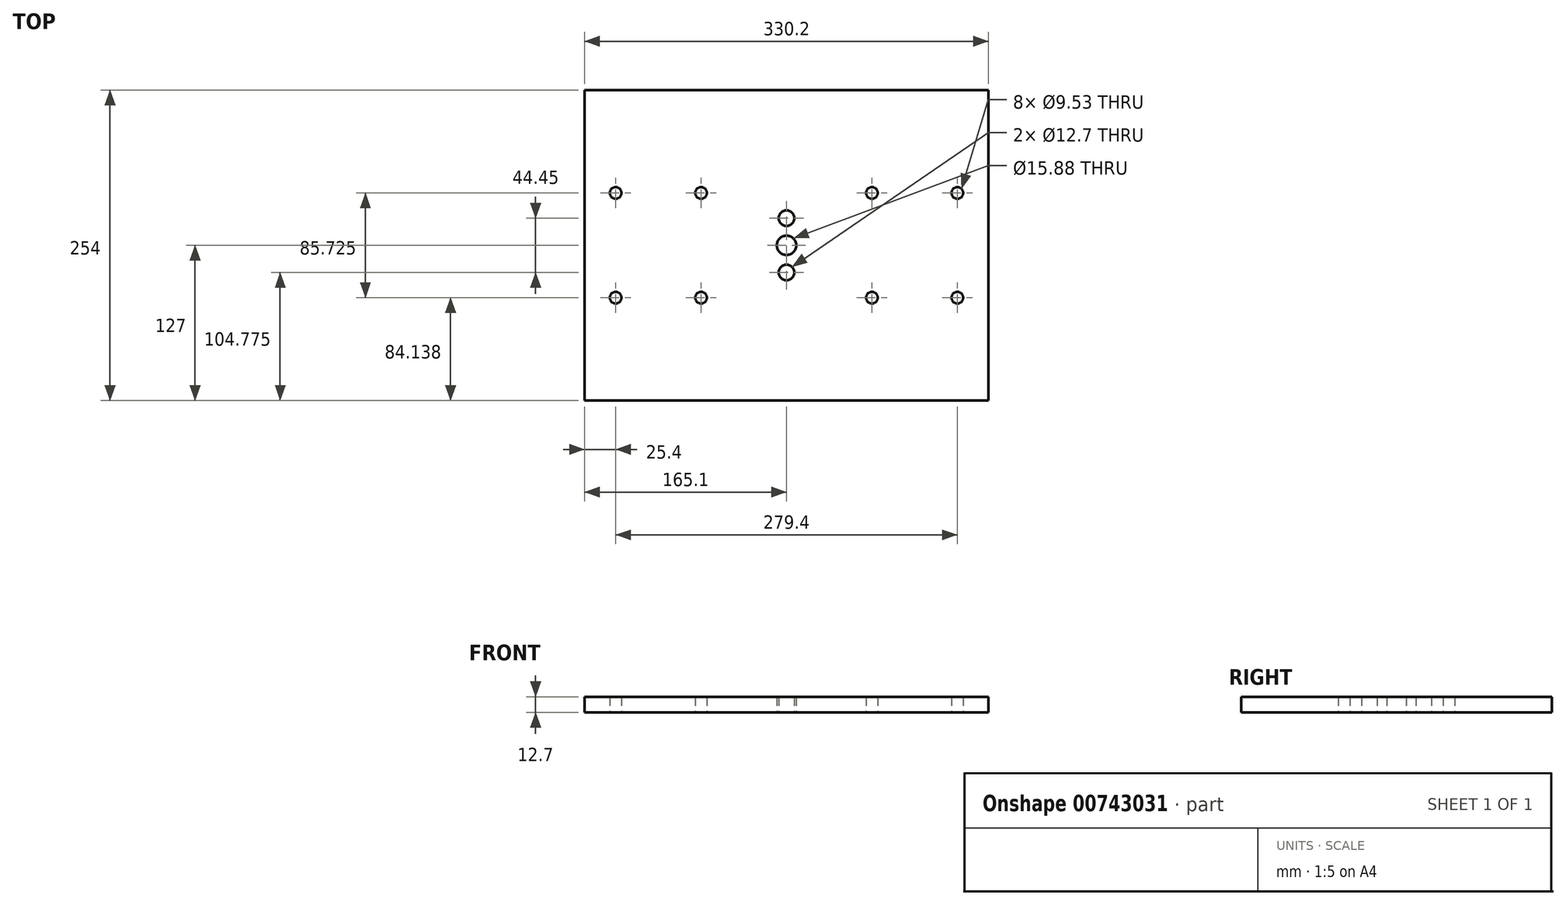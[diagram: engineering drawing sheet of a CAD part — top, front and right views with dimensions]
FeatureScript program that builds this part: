
annotation { "Feature Type Name" : "Feature", "Feature Type Description" : "" }
export const myFeature = defineFeature(function(context is Context, id is Id, definition is map)
    precondition{}
    {
        {
            var Q0;
            Q0=qCreatedBy(makeId("Top.planeOp"),FACE);
            var sketch = newSketch(context, id + "F0", { "sketchPlane" : qUnion([Q0])});
            skLineSegment(sketch, "E0.bottom", {"start": v(-165.1, -127) * mm, "end": v(165.1, -127) * mm});
            skLineSegment(sketch, "E0.top", {"start": v(-165.1, 127) * mm, "end": v(165.1, 127) * mm});
            skLineSegment(sketch, "E0.left", {"start": v(-165.1, -127) * mm, "end": v(-165.1, 127) * mm});
            skLineSegment(sketch, "E0.right", {"start": v(165.1, -127) * mm, "end": v(165.1, 127) * mm});
            skPoint(sketch, "E0.middle", {"position": v(0, 0) * mm});
            skSolve(sketch);
        }
        {
            var Q0;
            Q0=makeQuery(id+"F0.imprint","IMPRINT",FACE,{"disambiguationData":[TD([[makeQuery(id+"F0.imprint","IMPRINT",EDGE,{"derivedFrom":sQuery(id+"F0.wireOp",EDGE,"E0.bottom")}),1.0]])]});
            extrude(context, id + "F1", {"entities" : qUnion([Q0]), "depth" : 12.7 * mm, "offsetDistance" : 25.4 * mm, "symmetric" : true});
        }
        {
            var Q0;
            Q0=makeQuery(id+"F1.opExtrude","CAP_FACE",FACE,{"disambiguationData":[OSD([sQuery(id+"F0.wireOp",EDGE,"E0.bottom"),sQuery(id+"F0.wireOp",EDGE,"E0.top"),sQuery(id+"F0.wireOp",EDGE,"E0.left"),sQuery(id+"F0.wireOp",EDGE,"E0.right")])],"isStart":false});
            var sketch = newSketch(context, id + "F2", { "sketchPlane" : qUnion([Q0])});
            skPoint(sketch, "E1", {"position": v(-120.93, 68.36) * mm});
            skPoint(sketch, "E2", {"position": v(0, 22.22) * mm});
            skPoint(sketch, "E3", {"position": v(0, -22.23) * mm});
            skSolve(sketch);
        }
        {
            var Q0;
            Q0=sQuery(id+"F2.wireOp",VERTEX,"E2");
            var Q1;
            Q1=sQuery(id+"F2.wireOp",VERTEX,"E3");
            var Q2;
            Q2=makeQuery(id+"F1.opExtrude","SWEPT_BODY",BODY,{"disambiguationData":[OSD([sQuery(id+"F0.wireOp",EDGE,"E0.bottom"),sQuery(id+"F0.wireOp",EDGE,"E0.top"),sQuery(id+"F0.wireOp",EDGE,"E0.left"),sQuery(id+"F0.wireOp",EDGE,"E0.right")])]});
            hole(context, id + "F3", {"style" : HoleStyle.SIMPLE, "endStyle" : HoleEndStyle.THROUGH, "holeDiameter" : 12.7 * mm, "majorDiameter" : 6.35 * mm, "isTappedThrough" : true, "tappedDepth" : 12.7 * mm, "tapClearance" : 3, "locations" : qUnion([Q0, Q1]), "scope" : qUnion([Q2])});
        }
        {
            var Q0;
            Q0=makeQuery(id+"F1.opExtrude","CAP_FACE",FACE,{"disambiguationData":[OSD([sQuery(id+"F0.wireOp",EDGE,"E0.bottom"),sQuery(id+"F0.wireOp",EDGE,"E0.top"),sQuery(id+"F0.wireOp",EDGE,"E0.left"),sQuery(id+"F0.wireOp",EDGE,"E0.right")])],"isStart":false});
            var sketch = newSketch(context, id + "F4", { "sketchPlane" : qUnion([Q0])});
            skPoint(sketch, "E4", {"position": v(0, 0) * mm});
            skSolve(sketch);
        }
        {
            var Q0;
            Q0=sQuery(id+"F4.wireOp",VERTEX,"E4");
            var Q1;
            Q1=makeQuery(id+"F1.opExtrude","SWEPT_BODY",BODY,{"disambiguationData":[OSD([sQuery(id+"F0.wireOp",EDGE,"E0.bottom"),sQuery(id+"F0.wireOp",EDGE,"E0.top"),sQuery(id+"F0.wireOp",EDGE,"E0.left"),sQuery(id+"F0.wireOp",EDGE,"E0.right")])]});
            hole(context, id + "F5", {"style" : HoleStyle.SIMPLE, "endStyle" : HoleEndStyle.THROUGH, "holeDiameter" : 15.88 * mm, "majorDiameter" : 6.35 * mm, "isTappedThrough" : true, "tappedDepth" : 12.7 * mm, "tapClearance" : 3, "locations" : qUnion([Q0]), "scope" : qUnion([Q1])});
        }
        {
            var Q0;
            Q0=makeQuery(id+"F1.opExtrude","CAP_FACE",FACE,{"disambiguationData":[OSD([sQuery(id+"F0.wireOp",EDGE,"E0.bottom"),sQuery(id+"F0.wireOp",EDGE,"E0.top"),sQuery(id+"F0.wireOp",EDGE,"E0.left"),sQuery(id+"F0.wireOp",EDGE,"E0.right")])],"isStart":false});
            var sketch = newSketch(context, id + "F6", { "sketchPlane" : qUnion([Q0])});
            skPoint(sketch, "E5", {"position": v(-139.7, 42.86) * mm});
            skPoint(sketch, "E6", {"position": v(-139.7, -42.86) * mm});
            skPoint(sketch, "E7", {"position": v(-69.85, 42.86) * mm});
            skPoint(sketch, "E8", {"position": v(-69.85, -42.86) * mm});
            skPoint(sketch, "E9", {"position": v(0, 0) * mm});
            skPoint(sketch, "E10.MirrorP", {"position": v(139.7, 42.86) * mm});
            skPoint(sketch, "E11.MirrorP", {"position": v(69.85, 42.86) * mm});
            skPoint(sketch, "E12.MirrorP", {"position": v(69.85, -42.86) * mm});
            skPoint(sketch, "E13.MirrorP", {"position": v(139.7, -42.86) * mm});
            skSolve(sketch);
        }
        {
            var Q0;
            Q0=sQuery(id+"F6.wireOp",VERTEX,"E7");
            var Q1;
            Q1=sQuery(id+"F6.wireOp",VERTEX,"E5");
            var Q2;
            Q2=sQuery(id+"F6.wireOp",VERTEX,"E6");
            var Q3;
            Q3=sQuery(id+"F6.wireOp",VERTEX,"E8");
            var Q4;
            Q4=sQuery(id+"F6.wireOp",VERTEX,"E11.MirrorP");
            var Q5;
            Q5=sQuery(id+"F6.wireOp",VERTEX,"E10.MirrorP");
            var Q6;
            Q6=sQuery(id+"F6.wireOp",VERTEX,"E13.MirrorP");
            var Q7;
            Q7=sQuery(id+"F6.wireOp",VERTEX,"E12.MirrorP");
            var Q8;
            Q8=makeQuery(id+"F1.opExtrude","SWEPT_BODY",BODY,{"disambiguationData":[OSD([sQuery(id+"F0.wireOp",EDGE,"E0.bottom"),sQuery(id+"F0.wireOp",EDGE,"E0.top"),sQuery(id+"F0.wireOp",EDGE,"E0.left"),sQuery(id+"F0.wireOp",EDGE,"E0.right")])]});
            hole(context, id + "F7", {"style" : HoleStyle.SIMPLE, "endStyle" : HoleEndStyle.THROUGH, "holeDiameter" : 9.52 * mm, "majorDiameter" : 6.35 * mm, "isTappedThrough" : true, "tappedDepth" : 12.7 * mm, "tapClearance" : 3, "locations" : qUnion([Q0, Q1, Q2, Q3, Q4, Q5, Q6, Q7]), "scope" : qUnion([Q8])});
        }
    });
